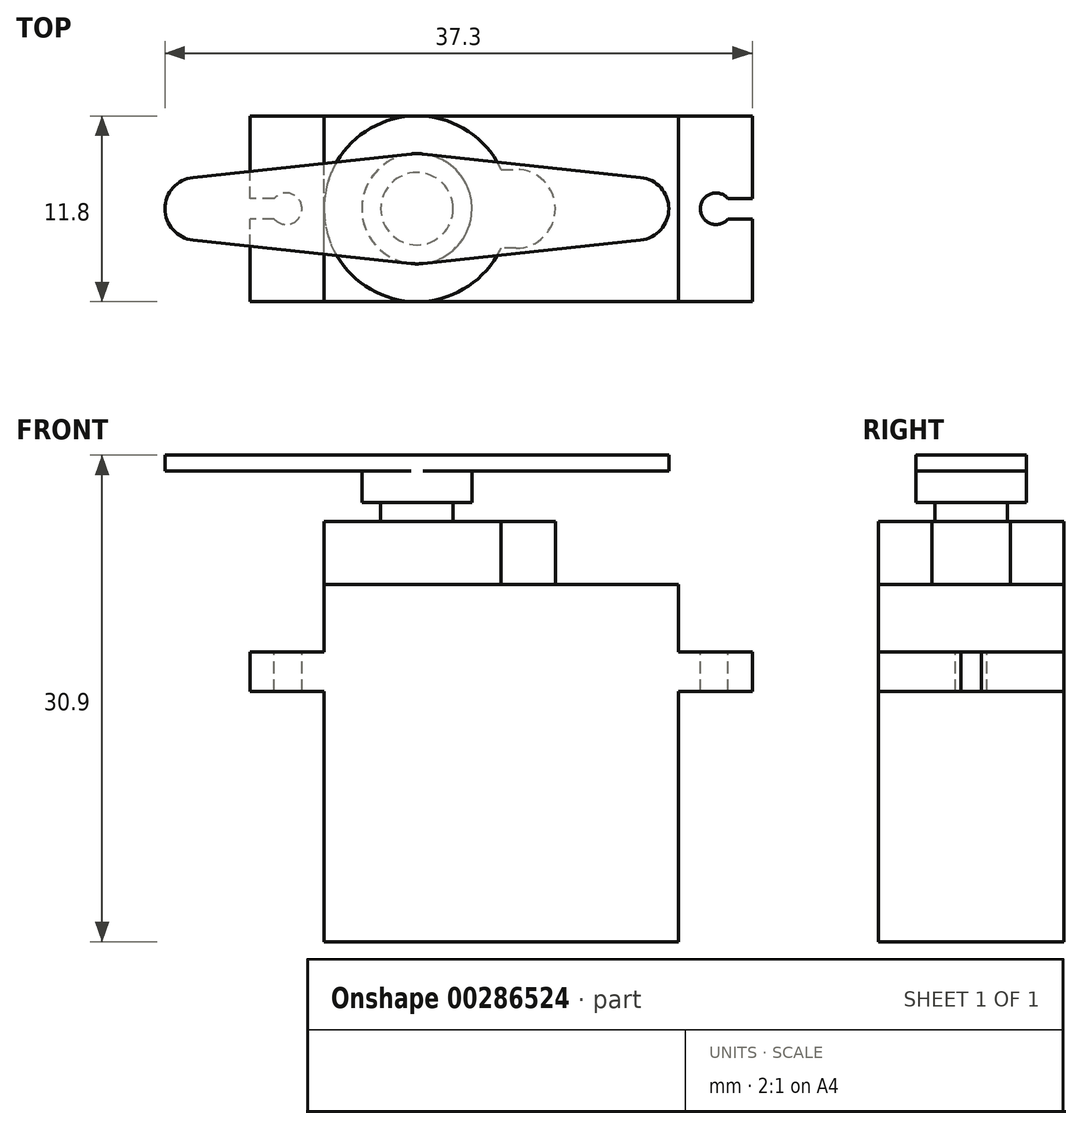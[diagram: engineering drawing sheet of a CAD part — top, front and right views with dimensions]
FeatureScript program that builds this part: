
annotation { "Feature Type Name" : "Feature", "Feature Type Description" : "" }
export const myFeature = defineFeature(function(context is Context, id is Id, definition is map)
    precondition{}
    {
        {
            var Q0;
            Q0=qCreatedBy(makeId("Front.planeOp"),FACE);
            var sketch = newSketch(context, id + "F0", { "sketchPlane" : qUnion([Q0])});
            skLineSegment(sketch, "E0.bottom", {"start": v(0, 0) * mm, "end": v(22.5, 0) * mm});
            skLineSegment(sketch, "E0.top", {"start": v(0, 22.7) * mm, "end": v(22.5, 22.7) * mm});
            skLineSegment(sketch, "E0.left", {"start": v(0, 0) * mm, "end": v(0, 22.7) * mm});
            skLineSegment(sketch, "E0.right", {"start": v(22.5, 0) * mm, "end": v(22.5, 22.7) * mm});
            skLineSegment(sketch, "E1.bottom", {"start": v(-4.7, 18.4) * mm, "end": v(27.2, 18.4) * mm});
            skLineSegment(sketch, "E1.top", {"start": v(-4.7, 15.9) * mm, "end": v(27.2, 15.9) * mm});
            skLineSegment(sketch, "E1.left", {"start": v(-4.7, 18.4) * mm, "end": v(-4.7, 15.9) * mm});
            skLineSegment(sketch, "E1.right", {"start": v(27.2, 18.4) * mm, "end": v(27.2, 15.9) * mm});
            skSolve(sketch);
        }
        {
            var Q0;
            Q0 = qSketchRegion(id + "F0", true);
            extrude(context, id + "F1", {"entities" : qUnion([Q0]), "depth" : 11.8 * mm, "offsetDistance" : 25 * mm});
        }
        {
            var Q0;
            Q0=makeQuery(id+"F1.opExtrude","SWEPT_FACE",FACE,{"disambiguationData":[OSD([sQuery(id+"F0.wireOp",EDGE,"E0.top")])]});
            var sketch = newSketch(context, id + "F2", { "sketchPlane" : qUnion([Q0])});
            skCircle(sketch, "E2", {"center": v(5.9, -5.9) * mm, "radius": 5.9 * mm});
            skPoint(sketch, "E2.centerSnap0", {"position": v(0, -5.9) * mm});
            skCircle(sketch, "E3", {"center": v(12.2, -5.9) * mm, "radius": 2.5 * mm});
            skLineSegment(sketch, "E4", {"start": v(12.2, -8.4) * mm, "end": v(11.24, -8.4) * mm});
            skLineSegment(sketch, "E5", {"start": v(11.24, -3.4) * mm, "end": v(12.2, -3.4) * mm});
            skSolve(sketch);
        }
        {
            var Q0;
            Q0 = qSketchRegion(id + "F2", true);
            var Q1;
            {var subQ0=sQuery(id+"F2.wireOp",EDGE,"E3");var subQ1=sQuery(id+"F2.wireOp",EDGE,"E2");var subQ2=makeQuery(id+"F2.imprint","INTERSECT",VERTEX,{"disambiguationData":[OD(0.0)],"derivedFrom":[subQ1,subQ0]});Q1=makeQuery(id+"F2.imprint","IMPRINT",FACE,{"disambiguationData":[TD([[makeQuery(id+"F2.imprint","IMPRINT",EDGE,{"disambiguationData":[TD([[subQ2,1.0]])],"derivedFrom":subQ1}),1.0]])]});}
            extrude(context, id + "F3", {"entities" : qUnion([Q0, Q1]), "operationType" : NewBodyOperationType.ADD, "depth" : 4 * mm, "offsetDistance" : 25 * mm});
        }
        {
            var Q0;
            {var subQ0=sQuery(id+"F0.wireOp",EDGE,"E1.bottom");Q0=makeQuery(id+"F1.opExtrude","SWEPT_FACE",FACE,{"disambiguationData":[OSD([subQ0]),TDD([makeQuery(id+"F0.imprint","IMPRINT",EDGE,{"disambiguationData":[TD([[makeQuery(id+"F0.imprint","INTERSECT",VERTEX,{"derivedFrom":[subQ0,sQuery(id+"F0.wireOp",EDGE,"E1.left")]}),-1.0]])],"derivedFrom":subQ0})])]});}
            var sketch = newSketch(context, id + "F4", { "sketchPlane" : qUnion([Q0])});
            skCircle(sketch, "E6", {"center": v(-2.4, -5.9) * mm, "radius": 1 * mm});
            skPoint(sketch, "E6.centerSnap0", {"position": v(-4.7, -5.9) * mm});
            skCircle(sketch, "E7", {"center": v(24.9, -5.9) * mm, "radius": 1 * mm});
            skLineSegment(sketch, "E8.bottom", {"start": v(-2.4, -5.25) * mm, "end": v(-7, -5.25) * mm});
            skLineSegment(sketch, "E8.top", {"start": v(-2.4, -6.55) * mm, "end": v(-7, -6.55) * mm});
            skLineSegment(sketch, "E8.left", {"start": v(-2.4, -5.25) * mm, "end": v(-2.4, -6.55) * mm});
            skLineSegment(sketch, "E8.right", {"start": v(-7, -5.25) * mm, "end": v(-7, -6.55) * mm});
            skLineSegment(sketch, "E9.bottom", {"start": v(24.9, -5.25) * mm, "end": v(29.55, -5.25) * mm});
            skLineSegment(sketch, "E9.top", {"start": v(24.9, -6.55) * mm, "end": v(29.55, -6.55) * mm});
            skLineSegment(sketch, "E9.left", {"start": v(24.9, -5.25) * mm, "end": v(24.9, -6.55) * mm});
            skLineSegment(sketch, "E9.right", {"start": v(29.55, -5.25) * mm, "end": v(29.55, -6.55) * mm});
            skPoint(sketch, "E9.middle", {"position": v(27.22, -5.9) * mm});
            skSolve(sketch);
        }
        {
            var Q0;
            Q0 = qSketchRegion(id + "F4", true);
            extrude(context, id + "F5", {"entities" : qUnion([Q0]), "operationType" : NewBodyOperationType.REMOVE, "endBound" : BoundingType.THROUGH_ALL, "oppositeDirection" : true, "depth" : 25 * mm, "offsetDistance" : 25 * mm});
        }
        {
            var Q0;
            Q0=makeQuery(id+"F3.opExtrude","CAP_FACE",FACE,{"disambiguationData":[OSD([sQuery(id+"F2.wireOp",EDGE,"E2"),sQuery(id+"F2.wireOp",EDGE,"E3"),sQuery(id+"F2.wireOp",EDGE,"E4"),sQuery(id+"F2.wireOp",EDGE,"E5")])],"isStart":false});
            var sketch = newSketch(context, id + "F6", { "sketchPlane" : qUnion([Q0])});
            skCircle(sketch, "E10", {"center": v(5.9, -5.9) * mm, "radius": 2.3 * mm});
            skSolve(sketch);
        }
        {
            var Q0;
            Q0 = qSketchRegion(id + "F6", true);
            extrude(context, id + "F7", {"entities" : qUnion([Q0]), "depth" : 3.2 * mm, "offsetDistance" : 25 * mm});
        }
        {
            var Q0;
            Q0=makeQuery(id+"F7.opExtrude","CAP_FACE",FACE,{"disambiguationData":[OSD([sQuery(id+"F6.wireOp",EDGE,"E10")])],"isStart":false});
            var sketch = newSketch(context, id + "F8", { "sketchPlane" : qUnion([Q0])});
            skCircle(sketch, "E11", {"center": v(5.9, -5.9) * mm, "radius": 3.5 * mm});
            skCircle(sketch, "E12", {"center": v(-8.1, -5.9) * mm, "radius": 2 * mm});
            skLineSegment(sketch, "E13", {"start": v(-8.31, -3.91) * mm, "end": v(5.53, -2.42) * mm});
            skLineSegment(sketch, "E14", {"start": v(5.9, -5.9) * mm, "end": v(5.9, -2.4) * mm, "construction": true});
            skLineSegment(sketch, "E15", {"start": v(5.9, -5.9) * mm, "end": v(2.4, -5.9) * mm, "construction": true});
            skLineSegment(sketch, "E16.MirrorCS", {"start": v(20.11, -3.91) * mm, "end": v(6.27, -2.42) * mm});
            skCircle(sketch, "E17.MirrorC", {"center": v(19.9, -5.9) * mm, "radius": 2 * mm});
            skLineSegment(sketch, "E18.MirrorCS", {"start": v(-8.31, -7.89) * mm, "end": v(5.53, -9.38) * mm});
            skLineSegment(sketch, "E19.MirrorCS", {"start": v(20.11, -7.89) * mm, "end": v(6.27, -9.38) * mm});
            skSolve(sketch);
        }
        {
            var Q0;
            Q0 = qSketchRegion(id + "F8", true);
            extrude(context, id + "F9", {"entities" : qUnion([Q0]), "operationType" : NewBodyOperationType.ADD, "depth" : 1 * mm, "offsetDistance" : 25 * mm});
        }
        {
            var Q0;
            Q0=makeQuery(id+"F8.imprint","IMPRINT",FACE,{"disambiguationData":[TD([[makeQuery(id+"F8.imprint","IMPRINT",EDGE,{"derivedFrom":makeQuery(id+"F7.opExtrude","CAP_EDGE",EDGE,{"disambiguationData":[OSD([sQuery(id+"F6.wireOp",EDGE,"E10")])],"isStart":false})}),-1.0]])]});
            extrude(context, id + "F10", {"entities" : qUnion([Q0]), "operationType" : NewBodyOperationType.ADD, "oppositeDirection" : true, "depth" : 2 * mm, "offsetDistance" : 25 * mm});
        }
    });
